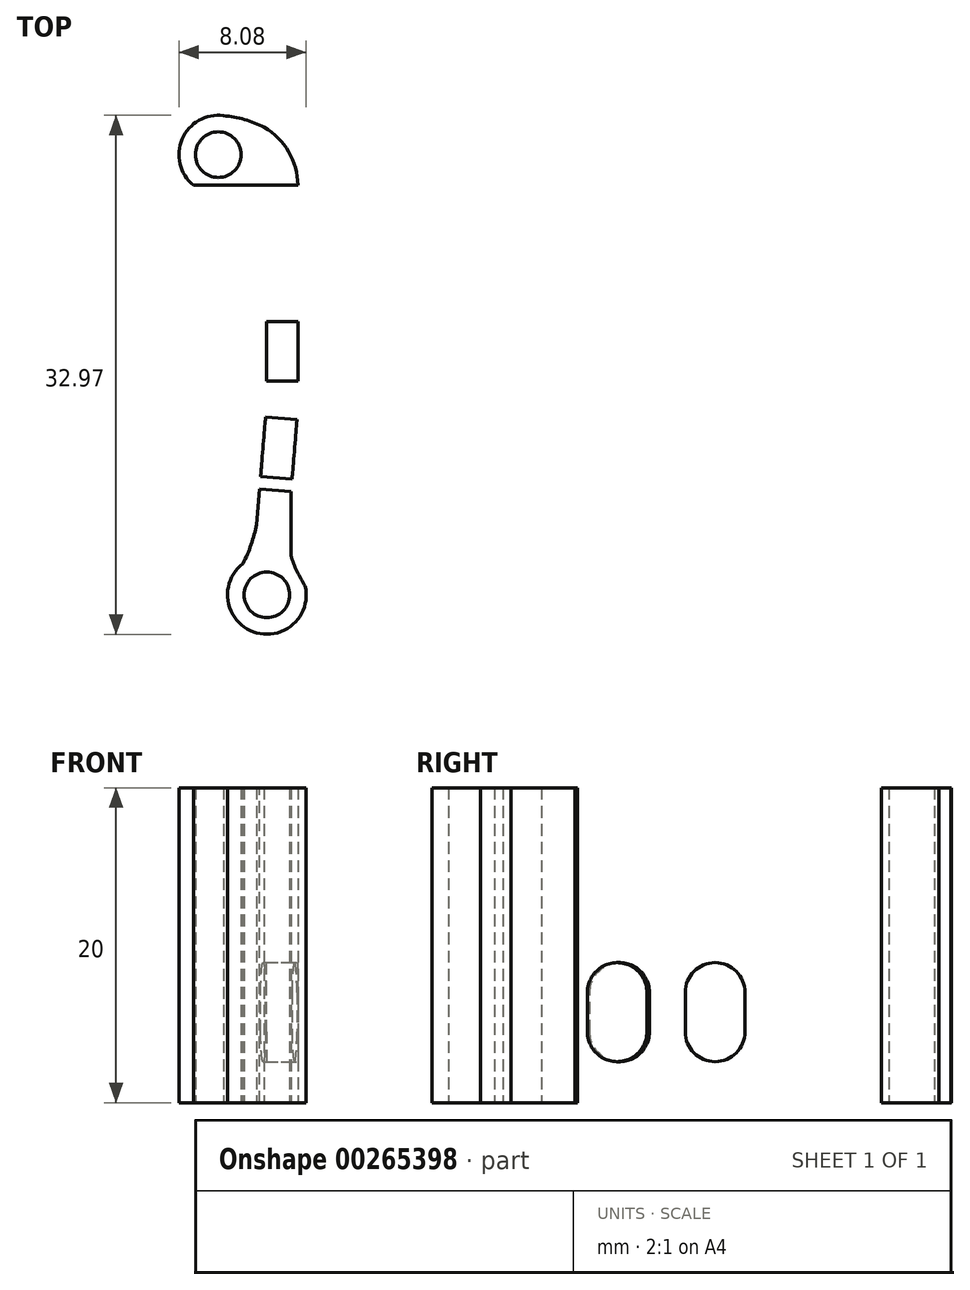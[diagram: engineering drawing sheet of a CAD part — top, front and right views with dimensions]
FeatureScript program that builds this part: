
annotation { "Feature Type Name" : "Feature", "Feature Type Description" : "" }
export const myFeature = defineFeature(function(context is Context, id is Id, definition is map)
    precondition{}
    {
        {
            var Q0;
            Q0=qCreatedBy(makeId("Top.planeOp"),FACE);
            var sketch = newSketch(context, id + "F0", { "sketchPlane" : qUnion([Q0])});
            skCircle(sketch, "E0", {"center": v(0.6, 14) * mm, "radius": 1.45 * mm});
            skCircle(sketch, "E1", {"center": v(3.68, -13.96) * mm, "radius": 1.45 * mm});
            skLineSegment(sketch, "E2", {"start": v(5.66, -2.04) * mm, "end": v(5.66, 12.07) * mm});
            skLineSegment(sketch, "E3", {"start": v(5.22, -7.39) * mm, "end": v(5.66, -2.04) * mm});
            skCircle(sketch, "E4", {"center": v(0.6, 14) * mm, "radius": 2.5 * mm});
            skLineSegment(sketch, "E5.0", {"start": v(3.66, -1.95) * mm, "end": v(3.66, 8.95) * mm});
            skLineSegment(sketch, "E6.0", {"start": v(3.22, -7.22) * mm, "end": v(3.66, -1.95) * mm});
            skArc(sketch, "E7", {"start": v(3.66, 8.95) * mm, "mid": v(2.71, 10.86) * mm, "end": v(0.68, 11.5) * mm});
            skPoint(sketch, "E8.end.orphan", {"position": v(0.6, 16.5) * mm});
            skArc(sketch, "E9", {"start": v(3.52, 15.74) * mm, "mid": v(2.1, 16.28) * mm, "end": v(0.6, 16.5) * mm});
            skArc(sketch, "E10", {"start": v(5.22, -11.47) * mm, "mid": v(5.6, -12.47) * mm, "end": v(6.12, -13.4) * mm});
            skArc(sketch, "E11", {"start": v(2.17, -11.97) * mm, "mid": v(2.68, -10.76) * mm, "end": v(3.04, -9.5) * mm});
            skArc(sketch, "E12", {"start": v(5.66, 12.07) * mm, "mid": v(5.07, 14.18) * mm, "end": v(3.52, 15.74) * mm});
            skArc(sketch, "E13", {"start": v(2.17, -11.97) * mm, "mid": v(2.83, -16.3) * mm, "end": v(6.12, -13.4) * mm});
            skLineSegment(sketch, "E14", {"start": v(5.22, -7.39) * mm, "end": v(5.22, -11.47) * mm});
            skLineSegment(sketch, "E15", {"start": v(3.22, -7.22) * mm, "end": v(3.04, -9.5) * mm});
            skPoint(sketch, "E15.endSnap0", {"position": v(2.95, -9.89) * mm});
            skSolve(sketch);
        }
        {
            var Q0;
            Q0 = qSketchRegion(id + "F0", true);
            extrude(context, id + "F1", {"entities" : qUnion([Q0]), "depth" : 20 * mm});
        }
        {
            var Q0;
            Q0=makeQuery(id+"F1.opExtrude","SWEPT_FACE",FACE,{"disambiguationData":[OSD([sQuery(id+"F0.wireOp",EDGE,"E2")])]});
            var sketch = newSketch(context, id + "F2", { "sketchPlane" : qUnion([Q0])});
            skLineSegment(sketch, "E16", {"start": v(5.02, 20) * mm, "end": v(5.02, 0) * mm, "construction": true});
            skLineSegment(sketch, "E17", {"start": v(12.07, 10) * mm, "end": v(-2.04, 10) * mm, "construction": true});
            skPoint(sketch, "E18", {"position": v(5.02, 10) * mm});
            skLineSegment(sketch, "E19.bottom", {"start": v(3.41, 15.5) * mm, "end": v(-0.38, 15.5) * mm, "construction": true});
            skLineSegment(sketch, "E19.top", {"start": v(3.41, 4.5) * mm, "end": v(-0.38, 4.5) * mm, "construction": true});
            skLineSegment(sketch, "E19.left", {"start": v(3.41, 15.5) * mm, "end": v(3.41, 13) * mm});
            skLineSegment(sketch, "E19.right", {"start": v(-0.38, 15.5) * mm, "end": v(-0.38, 13) * mm});
            skPoint(sketch, "E19.middle", {"position": v(1.52, 10) * mm});
            skArc(sketch, "E20", {"start": v(3.41, 15.5) * mm, "mid": v(1.52, 17.4) * mm, "end": v(-0.38, 15.5) * mm});
            skArc(sketch, "E21.MirrorCS", {"start": v(3.41, 4.5) * mm, "mid": v(1.52, 2.6) * mm, "end": v(-0.38, 4.5) * mm});
            skArc(sketch, "E22.MirrorCS", {"start": v(6.62, 4.5) * mm, "mid": v(8.52, 2.6) * mm, "end": v(10.41, 4.5) * mm});
            skLineSegment(sketch, "E23.MirrorCS", {"start": v(6.62, 15.5) * mm, "end": v(10.41, 15.5) * mm, "construction": true});
            skLineSegment(sketch, "E24.MirrorCS", {"start": v(6.62, 4.5) * mm, "end": v(10.41, 4.5) * mm, "construction": true});
            skLineSegment(sketch, "E25.MirrorCS", {"start": v(6.62, 15.5) * mm, "end": v(6.62, 13) * mm});
            skLineSegment(sketch, "E26.MirrorCS", {"start": v(10.41, 15.5) * mm, "end": v(10.41, 13) * mm});
            skArc(sketch, "E27.MirrorCS", {"start": v(6.62, 15.5) * mm, "mid": v(8.52, 17.4) * mm, "end": v(10.41, 15.5) * mm});
            skLineSegment(sketch, "E28", {"start": v(10.41, 13) * mm, "end": v(6.62, 13) * mm, "construction": true});
            skLineSegment(sketch, "E29", {"start": v(6.62, 7) * mm, "end": v(10.41, 7) * mm, "construction": true});
            skPoint(sketch, "E30", {"position": v(10.41, 10) * mm});
            skPoint(sketch, "E31", {"position": v(6.62, 10) * mm});
            skPoint(sketch, "E32", {"position": v(3.41, 10) * mm});
            skPoint(sketch, "E33", {"position": v(-0.38, 10) * mm});
            skLineSegment(sketch, "E34.trimOffspring", {"start": v(10.41, 7) * mm, "end": v(10.41, 4.5) * mm});
            skLineSegment(sketch, "E35.trimOffspring", {"start": v(6.62, 7) * mm, "end": v(6.62, 4.5) * mm});
            skArc(sketch, "E36", {"start": v(6.62, 13) * mm, "mid": v(8.52, 11.1) * mm, "end": v(10.41, 13) * mm});
            skArc(sketch, "E37", {"start": v(10.41, 7) * mm, "mid": v(8.52, 8.9) * mm, "end": v(6.62, 7) * mm});
            skArc(sketch, "E38.MirrorCS", {"start": v(-0.38, 7) * mm, "mid": v(1.52, 8.9) * mm, "end": v(3.41, 7) * mm});
            skArc(sketch, "E39.MirrorCS", {"start": v(3.41, 13) * mm, "mid": v(1.52, 11.1) * mm, "end": v(-0.38, 13) * mm});
            skLineSegment(sketch, "E40.trimOffspring", {"start": v(3.41, 7) * mm, "end": v(3.41, 4.5) * mm});
            skLineSegment(sketch, "E41.trimOffspring", {"start": v(-0.38, 7) * mm, "end": v(-0.38, 4.5) * mm});
            skSolve(sketch);
        }
        {
            var Q0;
            Q0=makeQuery(id+"F2.imprint","IMPRINT",FACE,{"disambiguationData":[TD([[makeQuery(id+"F2.imprint","IMPRINT",EDGE,{"derivedFrom":sQuery(id+"F2.wireOp",EDGE,"E19.left")}),-1.0]])]});
            var Q1;
            Q1=makeQuery(id+"F2.imprint","IMPRINT",FACE,{"disambiguationData":[TD([[makeQuery(id+"F2.imprint","IMPRINT",EDGE,{"derivedFrom":sQuery(id+"F2.wireOp",EDGE,"E22.MirrorCS")}),1.0]])]});
            var Q2;
            Q2=makeQuery(id+"F2.imprint","IMPRINT",FACE,{"disambiguationData":[TD([[makeQuery(id+"F2.imprint","IMPRINT",EDGE,{"derivedFrom":sQuery(id+"F2.wireOp",EDGE,"E25.MirrorCS")}),1.0]])]});
            var Q3;
            Q3=makeQuery(id+"F2.imprint","IMPRINT",FACE,{"disambiguationData":[TD([[makeQuery(id+"F2.imprint","IMPRINT",EDGE,{"derivedFrom":sQuery(id+"F2.wireOp",EDGE,"E21.MirrorCS")}),-1.0]])]});
            extrude(context, id + "F3", {"entities" : qUnion([Q0, Q1, Q2, Q3]), "operationType" : NewBodyOperationType.REMOVE, "oppositeDirection" : true, "depth" : 25 * mm, "offsetDistance" : 25 * mm});
        }
        {
            var Q0;
            Q0=makeQuery(id+"F1.opExtrude","SWEPT_FACE",FACE,{"disambiguationData":[OSD([sQuery(id+"F0.wireOp",EDGE,"E3")])]});
            var sketch = newSketch(context, id + "F4", { "sketchPlane" : qUnion([Q0])});
            skLineSegment(sketch, "E42", {"start": v(-1.56, 10) * mm, "end": v(-6.93, 10) * mm, "construction": true});
            skLineSegment(sketch, "E43.bottom", {"start": v(-2.35, 15.5) * mm, "end": v(-6.14, 15.5) * mm, "construction": true});
            skLineSegment(sketch, "E43.top", {"start": v(-2.35, 4.5) * mm, "end": v(-6.14, 4.5) * mm, "construction": true});
            skPoint(sketch, "E43.middle", {"position": v(-4.25, 10) * mm});
            skLineSegment(sketch, "E44", {"start": v(-4.25, 20) * mm, "end": v(-4.25, 0) * mm, "construction": true});
            skArc(sketch, "E45.MirrorCS", {"start": v(-2.35, 4.5) * mm, "mid": v(-4.25, 2.6) * mm, "end": v(-6.14, 4.5) * mm});
            skLineSegment(sketch, "E46.MirrorCS", {"start": v(-6.14, 15.5) * mm, "end": v(-6.14, 13) * mm});
            skLineSegment(sketch, "E47.MirrorCS", {"start": v(-2.35, 15.5) * mm, "end": v(-2.35, 13) * mm});
            skArc(sketch, "E48.MirrorCS", {"start": v(-6.14, 15.5) * mm, "mid": v(-4.25, 17.4) * mm, "end": v(-2.35, 15.5) * mm});
            skPoint(sketch, "E49", {"position": v(-2.35, 10) * mm});
            skPoint(sketch, "E50", {"position": v(-6.14, 10) * mm});
            skLineSegment(sketch, "E51.trimOffspring", {"start": v(-2.35, 7) * mm, "end": v(-2.35, 4.5) * mm});
            skLineSegment(sketch, "E52.trimOffspring", {"start": v(-6.14, 7) * mm, "end": v(-6.14, 4.5) * mm});
            skArc(sketch, "E53", {"start": v(-6.14, 13) * mm, "mid": v(-4.25, 11.1) * mm, "end": v(-2.35, 13) * mm});
            skArc(sketch, "E54", {"start": v(-2.35, 7) * mm, "mid": v(-4.25, 8.9) * mm, "end": v(-6.14, 7) * mm});
            skSolve(sketch);
        }
        {
            var Q0;
            Q0=makeQuery(id+"F4.imprint","IMPRINT",FACE,{"disambiguationData":[TD([[makeQuery(id+"F4.imprint","IMPRINT",EDGE,{"derivedFrom":sQuery(id+"F4.wireOp",EDGE,"E43.left")}),-1.0]])]});
            var Q1;
            Q1=makeQuery(id+"F4.imprint","IMPRINT",FACE,{"disambiguationData":[TD([[makeQuery(id+"F4.imprint","IMPRINT",EDGE,{"derivedFrom":sQuery(id+"F4.wireOp",EDGE,"E46.MirrorCS")}),1.0]])]});
            var Q2;
            Q2=makeQuery(id+"F4.imprint","IMPRINT",FACE,{"disambiguationData":[TD([[makeQuery(id+"F4.imprint","IMPRINT",EDGE,{"derivedFrom":sQuery(id+"F4.wireOp",EDGE,"E45.MirrorCS")}),-1.0]])]});
            extrude(context, id + "F5", {"entities" : qUnion([Q0, Q1, Q2]), "operationType" : NewBodyOperationType.REMOVE, "oppositeDirection" : true, "depth" : 25 * mm, "offsetDistance" : 25 * mm});
        }
    });
